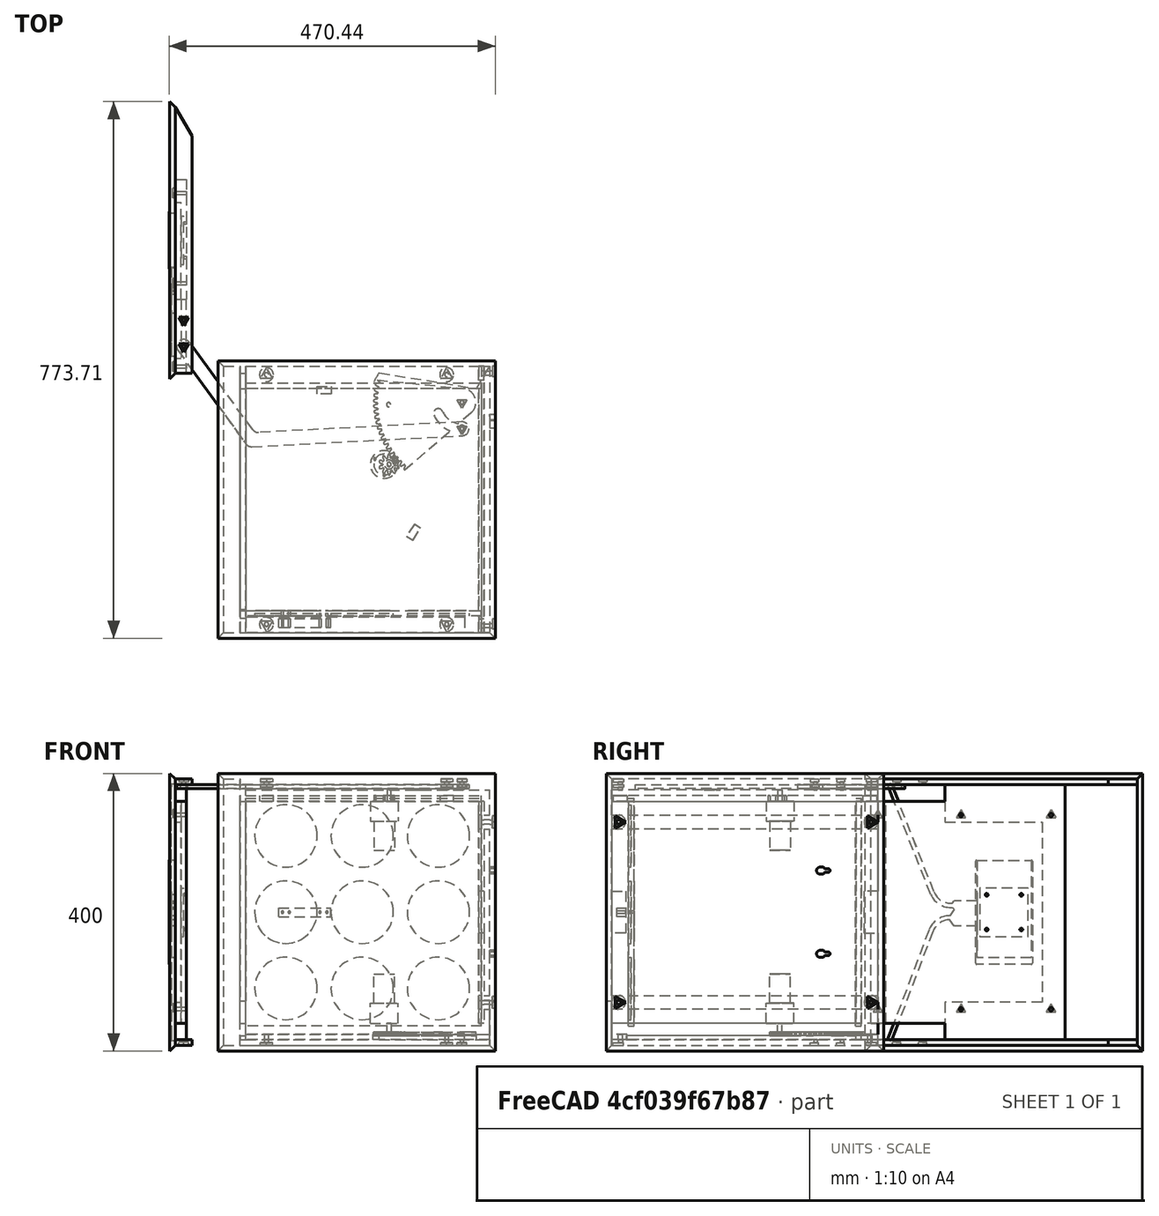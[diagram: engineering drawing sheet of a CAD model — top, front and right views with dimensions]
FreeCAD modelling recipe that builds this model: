
FCSTD DOCUMENT  (FreeCAD 0.16R6707 (Git))
Label: Latskap-animation
License: All rights reserved
LicenseURL: http://en.wikipedia.org/wiki/All_rights_reserved
objects: App::FeaturePython×23, Part::FeaturePython×8
note: 8 computed .brp shape members not serialized (recipe doc carries the construction recipe); baked Part::Feature solids carry a one-line shape summary decoded from their .brp

FEATURE [Part::FeaturePython] Latskap_base_01  # a2plus imported part (geometry in sourceFile) (typed FeaturePython)
  fixedPosition = true
  sourceFile = <userpath>/workspace/latskap/models/Latskap-base.fcstd
  timeLastImport = 1.50222e+09
  updateColors = true
FEATURE [Part::FeaturePython] Latskap_arm_upper_01  # a2plus imported part (geometry in sourceFile) (typed FeaturePython)
  Placement = pos=(31.8372,342.484,0) rot=(0,0,-1;0.942478rad)
  fixedPosition = false
  sourceFile = <userpath>/workspace/latskap/models/Latskap-arm-upper.fcstd
  timeLastImport = 1.50222e+09
  updateColors = true
FEATURE [Part::FeaturePython] Latskap_arm_lower_01  # a2plus imported part (geometry in sourceFile) (typed FeaturePython)
  Placement = pos=(62.5799,326.82,16) rot=(0,0,-1;0.942478rad)
  fixedPosition = false
  sourceFile = <userpath>/workspace/latskap/models/Latskap-arm-lower.fcstd
  timeLastImport = 1.50222e+09
  updateColors = true
FEATURE [Part::FeaturePython] Latskap_gear_small_01  # a2plus imported part (geometry in sourceFile) (typed FeaturePython)
  Placement = pos=(246.8,50.5,22) rot=(0,0,1;0.947714rad)
  fixedPosition = false
  sourceFile = <userpath>/workspace/latskap/models/Latskap-gear-small.fcstd
  timeLastImport = 1.50222e+09
  updateColors = true
FEATURE [Part::FeaturePython] Latskap_gear_big_01  # a2plus imported part (geometry in sourceFile) (typed FeaturePython)
  Placement = pos=(352,140,22) rot=(0,0,-1;0.144396rad)
  fixedPosition = false
  sourceFile = <userpath>/workspace/latskap/models/Latskap-gear-big.fcstd
  timeLastImport = 1.50223e+09
  updateColors = true
FEATURE [App::FeaturePython] circularEdgeConstraint01  label="circularEdgeConstraint01__Latskap_base_01"  # a2plus constraint (typed FeaturePython)
  Object1 = Latskap_arm_upper_01
  Object2 = Latskap_base_01
  SubElement1 = Edge26
  SubElement2 = Edge336
  Type = circularEdge
  directionConstraint = 0
  lockRotation = false
  offset = 0
FEATURE [App::FeaturePython] circularEdgeConstraint01_mirror  label="circularEdgeConstraint01__Latskap_arm_upper_01"  # a2plus constraint (typed FeaturePython)
  Object1 = Latskap_arm_upper_01
  Object2 = Latskap_base_01
  SubElement1 = Edge26
  SubElement2 = Edge336
  Type = circularEdge
  directionConstraint = 0
  lockRotation = false
  offset = 0
FEATURE [App::FeaturePython] circularEdgeConstraint02  label="circularEdgeConstraint02__Latskap_base_01"  # a2plus constraint (typed FeaturePython)
  Object1 = Latskap_arm_lower_01
  Object2 = Latskap_base_01
  SubElement1 = Edge26
  SubElement2 = Edge337
  Type = circularEdge
  directionConstraint = 0
  lockRotation = false
  offset = 0
FEATURE [App::FeaturePython] circularEdgeConstraint02_mirror  label="circularEdgeConstraint02__Latskap_arm_lower_01"  # a2plus constraint (typed FeaturePython)
  Object1 = Latskap_arm_lower_01
  Object2 = Latskap_base_01
  SubElement1 = Edge26
  SubElement2 = Edge337
  Type = circularEdge
  directionConstraint = 0
  lockRotation = false
  offset = 0
FEATURE [App::FeaturePython] circularEdgeConstraint03  label="circularEdgeConstraint03__Latskap_arm_upper_01"  # a2plus constraint (typed FeaturePython)
  Object1 = Latskap_gear_big_01
  Object2 = Latskap_arm_upper_01
  SubElement1 = Edge116
  SubElement2 = Edge27
  Type = circularEdge
  directionConstraint = 0
  lockRotation = false
  offset = 0
FEATURE [App::FeaturePython] circularEdgeConstraint03_mirror  label="circularEdgeConstraint03__Latskap_gear_big_01"  # a2plus constraint (typed FeaturePython)
  Object1 = Latskap_gear_big_01
  Object2 = Latskap_arm_upper_01
  SubElement1 = Edge116
  SubElement2 = Edge27
  Type = circularEdge
  directionConstraint = 0
  lockRotation = false
  offset = 0
FEATURE [App::FeaturePython] angleConstraint01  label="angleConstraint01__Latskap_arm_upper_01"  # a2plus constraint (typed FeaturePython)
  Object1 = Latskap_gear_big_01
  Object2 = Latskap_arm_upper_01
  SubElement1 = Face14
  SubElement2 = Face7
  Type = angle_between_planes
  angle = 8.7
FEATURE [App::FeaturePython] angleConstraint01_mirror  label="angleConstraint01__Latskap_gear_big_01"  # a2plus constraint (typed FeaturePython)
  Object1 = Latskap_gear_big_01
  Object2 = Latskap_arm_upper_01
  SubElement1 = Face14
  SubElement2 = Face7
  Type = angle_between_planes
  angle = 8.7
FEATURE [App::FeaturePython] angleConstraint02  label="angleConstraint02__Latskap_base_01"  # a2plus constraint (typed FeaturePython)
  Object1 = Latskap_arm_upper_01
  Object2 = Latskap_base_01
  SubElement1 = Face7
  SubElement2 = Face193
  Type = angle_between_planes
  a = 180
  a_0_animatation = 0
  a_1_animatation = 180
  a_n_animatation = 84
  angle = -3
  animation_exp_animatation = -57+53*sin(a)
  interp_method_animatation = none
  loop_animatation = true
  n_interp_animatation = 6
  play_after_generate_animatation = false
  timer_ms_animatation = 25
  expr: angle = -57 + 53 * sin(a)
FEATURE [App::FeaturePython] angleConstraint02_mirror  label="angleConstraint02__Latskap_arm_upper_01"  # a2plus constraint (typed FeaturePython)
  Object1 = Latskap_arm_upper_01
  Object2 = Latskap_base_01
  SubElement1 = Face7
  SubElement2 = Face193
  Type = angle_between_planes
  angle = -3
  expr: angle = -3
FEATURE [App::FeaturePython] angleConstraint03  label="angleConstraint03__Latskap_arm_upper_01"  # a2plus constraint (typed FeaturePython)
  Object1 = Latskap_arm_lower_01
  Object2 = Latskap_arm_upper_01
  SubElement1 = Face7
  SubElement2 = Face7
  Type = angle_between_planes
  angle = 0
FEATURE [App::FeaturePython] angleConstraint03_mirror  label="angleConstraint03__Latskap_arm_lower_01"  # a2plus constraint (typed FeaturePython)
  Object1 = Latskap_arm_lower_01
  Object2 = Latskap_arm_upper_01
  SubElement1 = Face7
  SubElement2 = Face7
  Type = angle_between_planes
  angle = 0
FEATURE [App::FeaturePython] angleConstraint04  label="angleConstraint04__Latskap_gear_big_01"  # a2plus constraint (typed FeaturePython)
  Object1 = Latskap_gear_small_01
  Object2 = Latskap_gear_big_01
  SubElement1 = Face83
  SubElement2 = Face14
  Type = angle_between_planes
  angle = 30
  expr: angle = -10 * angleConstraint02.angle / deg
FEATURE [App::FeaturePython] angleConstraint04_mirror  label="angleConstraint04__Latskap_gear_small_01"  # a2plus constraint (typed FeaturePython)
  Object1 = Latskap_gear_small_01
  Object2 = Latskap_gear_big_01
  SubElement1 = Face83
  SubElement2 = Face14
  Type = angle_between_planes
  angle = 30
FEATURE [Part::FeaturePython] Latskap_door_01  # a2plus imported part (geometry in sourceFile) (typed FeaturePython)
  Placement = pos=(-69.444,373.708,0) rot=(0,0,1;0rad)
  fixedPosition = false
  sourceFile = <userpath>/workspace/latskap/models/Latskap-door.fcstd
  timeLastImport = 1.50223e+09
  updateColors = true
FEATURE [App::FeaturePython] circularEdgeConstraint04  label="circularEdgeConstraint04__Latskap_door_01"  # a2plus constraint (typed FeaturePython)
  Object1 = Latskap_arm_lower_01
  Object2 = Latskap_door_01
  SubElement1 = Edge29
  SubElement2 = Edge96
  Type = circularEdge
  directionConstraint = 0
  lockRotation = false
  offset = 0
FEATURE [App::FeaturePython] circularEdgeConstraint04_mirror  label="circularEdgeConstraint04__Latskap_arm_lower_01"  # a2plus constraint (typed FeaturePython)
  Object1 = Latskap_arm_lower_01
  Object2 = Latskap_door_01
  SubElement1 = Edge29
  SubElement2 = Edge96
  Type = circularEdge
  directionConstraint = 0
  lockRotation = false
  offset = 0
FEATURE [Part::FeaturePython] Clone  label="Clone of Latskap_arm_upper_01"  # Draft clone (typed FeaturePython)
  Objects = -> [Latskap_arm_upper_01]
  Placement = pos=(31.8372,342.484,362) rot=(0,0,-1;0.942478rad)
  Scale = (1,1,1)
FEATURE [Part::FeaturePython] Clone001  label="Clone of Latskap_arm_lower_01"  # Draft clone (typed FeaturePython)
  Objects = -> [Latskap_arm_lower_01]
  Placement = pos=(62.5799,326.82,378) rot=(0,0,-1;0.942478rad)
  Scale = (1,1,1)
FEATURE [App::FeaturePython] angleConstraint05  label="angleConstraint05__Latskap_arm_upper_01"  # a2plus constraint (typed FeaturePython)
  Object1 = Clone
  Object2 = Latskap_arm_upper_01
  SubElement1 = Face7
  SubElement2 = Face7
  Type = angle_between_planes
  angle = 0
FEATURE [App::FeaturePython] angleConstraint05_mirror  label="angleConstraint05__Clone of Latskap_arm_upper_01"  # a2plus constraint (typed FeaturePython)
  Object1 = Clone
  Object2 = Latskap_arm_upper_01
  SubElement1 = Face7
  SubElement2 = Face7
  Type = angle_between_planes
  angle = 0
FEATURE [App::FeaturePython] circularEdgeConstraint05  label="circularEdgeConstraint05__Clone of Latskap_arm_upper_01"  # a2plus constraint (typed FeaturePython)
  Object1 = Latskap_base_01
  Object2 = Clone
  SubElement1 = Edge753
  SubElement2 = Edge27
  Type = circularEdge
  directionConstraint = 0
  lockRotation = false
  offset = 0
FEATURE [App::FeaturePython] circularEdgeConstraint05_mirror  label="circularEdgeConstraint05__Latskap_base_01"  # a2plus constraint (typed FeaturePython)
  Object1 = Latskap_base_01
  Object2 = Clone
  SubElement1 = Edge753
  SubElement2 = Edge27
  Type = circularEdge
  directionConstraint = 0
  lockRotation = false
  offset = 0
FEATURE [App::FeaturePython] circularEdgeConstraint06  label="circularEdgeConstraint06__Latskap_base_01"  # a2plus constraint (typed FeaturePython)
  Object1 = Clone001
  Object2 = Latskap_base_01
  SubElement1 = Edge27
  SubElement2 = Edge754
  Type = circularEdge
  directionConstraint = 0
  lockRotation = false
  offset = 0
FEATURE [App::FeaturePython] circularEdgeConstraint06_mirror  label="circularEdgeConstraint06__Clone of Latskap_arm_lower_01"  # a2plus constraint (typed FeaturePython)
  Object1 = Clone001
  Object2 = Latskap_base_01
  SubElement1 = Edge27
  SubElement2 = Edge754
  Type = circularEdge
  directionConstraint = 0
  lockRotation = false
  offset = 0
FEATURE [App::FeaturePython] angleConstraint06  # a2plus constraint (typed FeaturePython)
  Object1 = Clone
  Object2 = Clone001
  SubElement1 = Face1
  SubElement2 = Face1
  Type = angle_between_planes
  angle = 0
